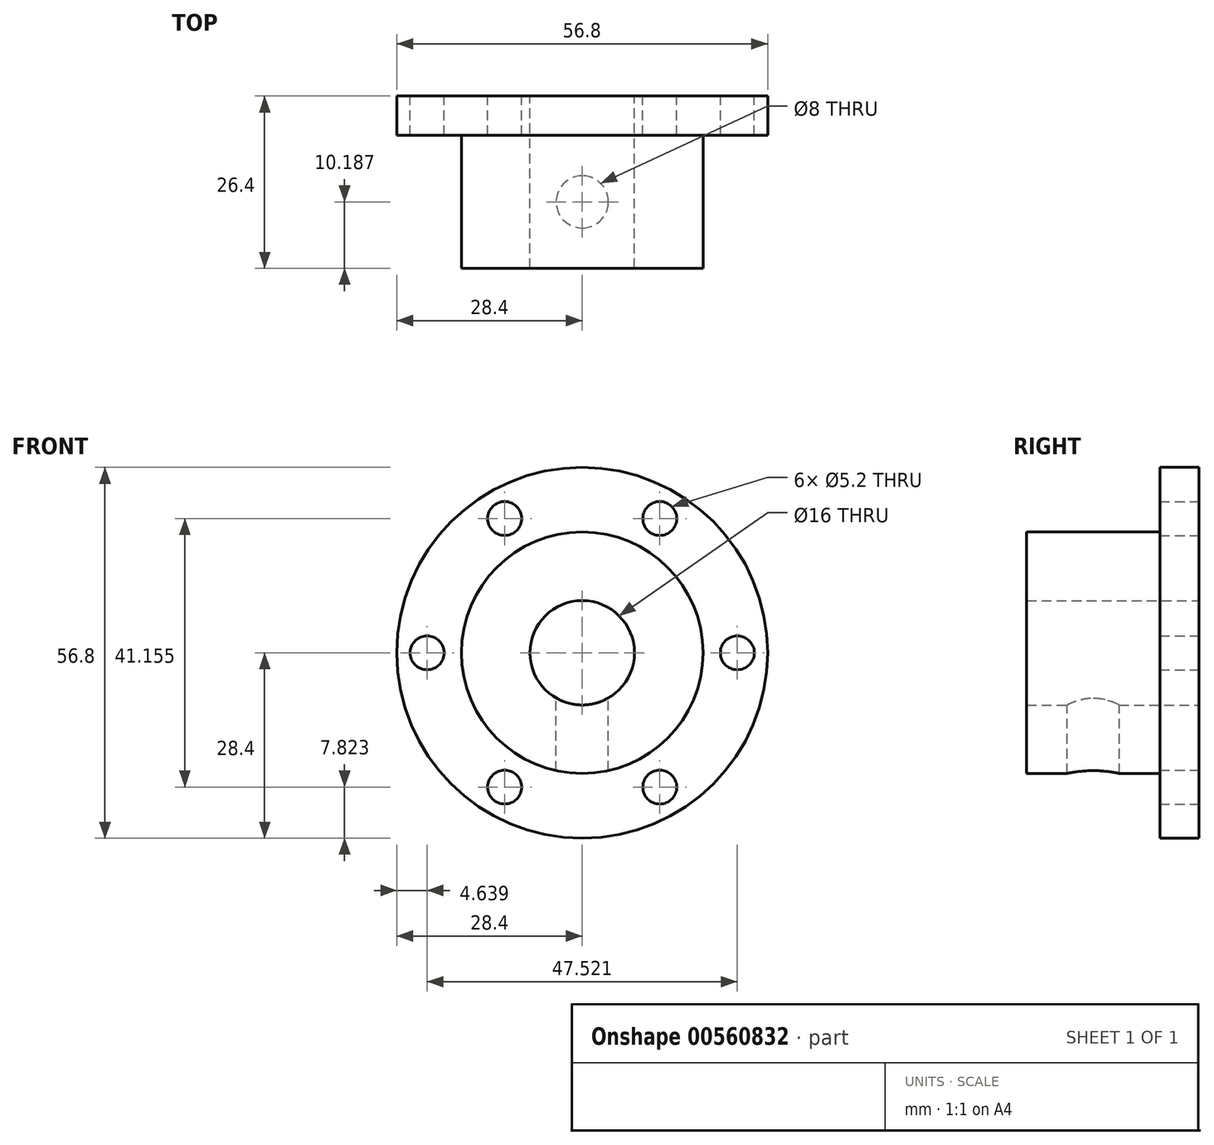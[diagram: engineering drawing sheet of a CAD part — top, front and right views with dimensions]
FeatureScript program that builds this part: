
annotation { "Feature Type Name" : "Feature", "Feature Type Description" : "" }
export const myFeature = defineFeature(function(context is Context, id is Id, definition is map)
    precondition{}
    {
        {
            var Q0;
            Q0=qCreatedBy(makeId("Front.planeOp"),FACE);
            var sketch = newSketch(context, id + "F0", { "sketchPlane" : qUnion([Q0])});
            skCircle(sketch, "E0", {"center": v(0, 0) * mm, "radius": 8 * mm});
            skSolve(sketch);
        }
        {
            var Q0;
            Q0=qCreatedBy(makeId("Front.planeOp"),FACE);
            var sketch = newSketch(context, id + "F1", { "sketchPlane" : qUnion([Q0])});
            skCircle(sketch, "E1", {"center": v(0, 0) * mm, "radius": 18.5 * mm});
            skCircle(sketch, "E2", {"center": v(0, 0) * mm, "radius": 23.75 * mm, "construction": true});
            skSolve(sketch);
        }
        {
            var Q0;
            Q0=qCreatedBy(makeId("Front.planeOp"),FACE);
            var sketch = newSketch(context, id + "F2", { "sketchPlane" : qUnion([Q0])});
            skCircle(sketch, "E3", {"center": v(0, 0) * mm, "radius": 28.4 * mm});
            skSolve(sketch);
        }
        {
            var Q0;
            Q0=qCreatedBy(makeId("Front.planeOp"),FACE);
            var sketch = newSketch(context, id + "F3", { "sketchPlane" : qUnion([Q0])});
            skCircle(sketch, "E4", {"center": v(-23.76, 0) * mm, "radius": 2.6 * mm});
            skCircle(sketch, "E5.1.0", {"center": v(-11.88, -20.58) * mm, "radius": 2.6 * mm});
            skCircle(sketch, "E5.2.0", {"center": v(11.88, -20.58) * mm, "radius": 2.6 * mm});
            skCircle(sketch, "E5.3.0", {"center": v(23.76, 0) * mm, "radius": 2.6 * mm});
            skCircle(sketch, "E5.4.0", {"center": v(11.88, 20.58) * mm, "radius": 2.6 * mm});
            skCircle(sketch, "E5.5.0", {"center": v(-11.88, 20.58) * mm, "radius": 2.6 * mm});
            skPoint(sketch, "E5.center", {"position": v(0, 0) * mm});
            skSolve(sketch);
        }
        {
            var Q0;
            Q0=qSketchRegion(id+"F1",true);
            extrude(context, id + "F4", {"entities" : qUnion([Q0]), "depth" : 26.4 * mm, "offsetDistance" : 25 * mm});
        }
        {
            var Q0;
            Q0=qSketchRegion(id+"F2",true);
            extrude(context, id + "F5", {"entities" : qUnion([Q0]), "operationType" : NewBodyOperationType.ADD, "depth" : 6 * mm, "offsetDistance" : 25 * mm});
        }
        {
            var Q0;
            Q0=makeQuery(id+"F0.imprint","IMPRINT",FACE,{"disambiguationData":[TD([[makeQuery(id+"F0.imprint","IMPRINT",EDGE,{"derivedFrom":sQuery(id+"F0.wireOp",EDGE,"E0")}),1.0]])]});
            var Q1;
            Q1=sQuery(id+"F0.wireOp",EDGE,"E0");
            extrude(context, id + "F6", {"entities" : qUnion([Q0]), "operationType" : NewBodyOperationType.REMOVE, "surfaceEntities" : qUnion([Q1]), "depth" : 26.4 * mm, "offsetDistance" : 25 * mm});
        }
        {
            var Q0;
            Q0=qSketchRegion(id+"F3",true);
            extrude(context, id + "F7", {"entities" : qUnion([Q0]), "operationType" : NewBodyOperationType.REMOVE, "depth" : 6 * mm, "offsetDistance" : 25 * mm});
        }
        {
            var Q0;
            Q0=qCreatedBy(makeId("Top.planeOp"),FACE);
            var sketch = newSketch(context, id + "F8", { "sketchPlane" : qUnion([Q0])});
            skCircle(sketch, "E6", {"center": v(0, -16.21) * mm, "radius": 4 * mm});
            skSolve(sketch);
        }
        {
            var Q0;
            Q0=qSketchRegion(id+"F8",true);
            extrude(context, id + "F9", {"entities" : qUnion([Q0]), "operationType" : NewBodyOperationType.REMOVE, "oppositeDirection" : true, "depth" : 28 * mm, "offsetDistance" : 25 * mm});
        }
    });
